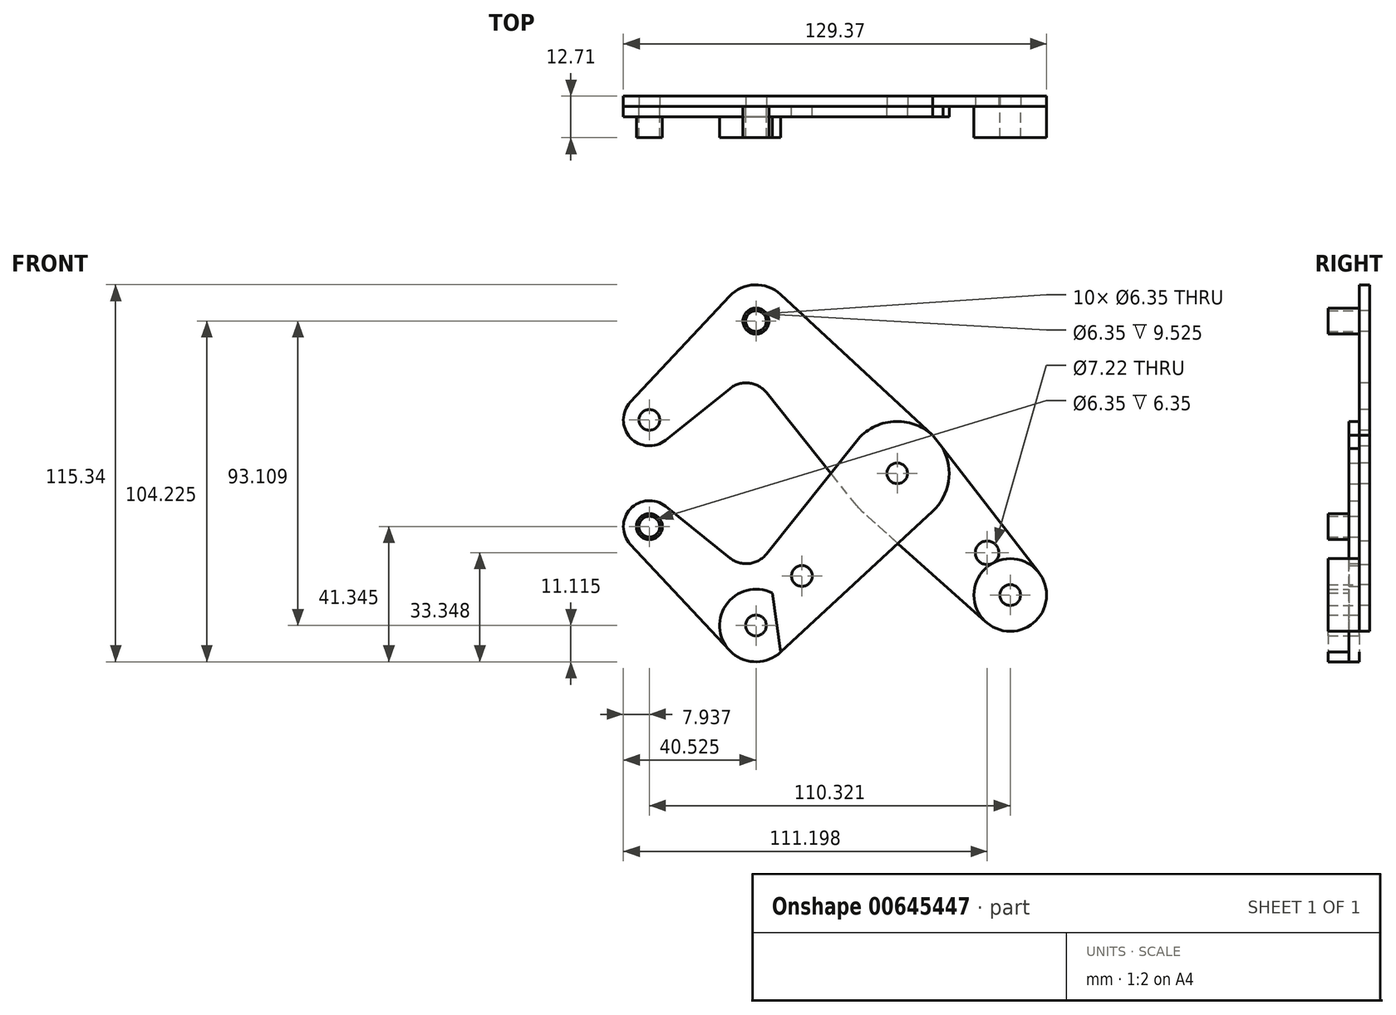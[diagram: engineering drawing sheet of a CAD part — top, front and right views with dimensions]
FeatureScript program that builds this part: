
annotation { "Feature Type Name" : "Feature", "Feature Type Description" : "" }
export const myFeature = defineFeature(function(context is Context, id is Id, definition is map)
    precondition{}
    {
        {
            var Q0;
            Q0=qCreatedBy(makeId("Front.planeOp"),FACE);
            var sketch = newSketch(context, id + "F0", { "sketchPlane" : qUnion([Q0])});
            skCircle(sketch, "E0", {"center": v(0, 0) * mm, "radius": 15.88 * mm});
            skLineSegment(sketch, "E1", {"start": v(0, 0) * mm, "end": v(-43.18, 46.55) * mm, "construction": true});
            skLineSegment(sketch, "E2", {"start": v(0, 0) * mm, "end": v(34.55, -37.24) * mm, "construction": true});
            skLineSegment(sketch, "E3", {"start": v(-43.18, 46.55) * mm, "end": v(-75.77, 16.33) * mm, "construction": true});
            skCircle(sketch, "E4", {"center": v(-43.18, 46.55) * mm, "radius": 11.11 * mm});
            skCircle(sketch, "E5", {"center": v(34.55, -37.24) * mm, "radius": 11.11 * mm});
            skCircle(sketch, "E6", {"center": v(34.55, -37.24) * mm, "radius": 3.18 * mm});
            skCircle(sketch, "E7", {"center": v(-75.77, 16.33) * mm, "radius": 7.94 * mm});
            skCircle(sketch, "E8", {"center": v(-43.18, 46.55) * mm, "radius": 3.18 * mm});
            skCircle(sketch, "E9", {"center": v(-75.77, 16.33) * mm, "radius": 3.18 * mm});
            skLineSegment(sketch, "E10", {"start": v(-81.57, 21.74) * mm, "end": v(-51.3, 54.14) * mm});
            skLineSegment(sketch, "E11", {"start": v(-35.63, 54.7) * mm, "end": v(10.8, 11.64) * mm});
            skLineSegment(sketch, "E12", {"start": v(10.8, 11.64) * mm, "end": v(43.34, -30.45) * mm});
            skLineSegment(sketch, "E13", {"start": v(0, 0) * mm, "end": v(-43.18, -46.55) * mm, "construction": true});
            skLineSegment(sketch, "E14", {"start": v(-43.18, -46.55) * mm, "end": v(-75.77, -16.33) * mm, "construction": true});
            skCircle(sketch, "E15", {"center": v(0, 0) * mm, "radius": 3.98 * mm});
            skCircle(sketch, "E16", {"center": v(0, 0) * mm, "radius": 3.18 * mm});
            skCircle(sketch, "E17", {"center": v(-43.18, -46.55) * mm, "radius": 11.11 * mm});
            skCircle(sketch, "E18", {"center": v(-43.18, -46.55) * mm, "radius": 3.18 * mm});
            skCircle(sketch, "E19", {"center": v(-75.77, -16.33) * mm, "radius": 7.94 * mm});
            skCircle(sketch, "E20", {"center": v(-75.77, -16.33) * mm, "radius": 3.18 * mm});
            skLineSegment(sketch, "E21", {"start": v(-70.8, 10.14) * mm, "end": v(-51.15, 25.91) * mm});
            skLineSegment(sketch, "E22", {"start": v(-12.42, -9.9) * mm, "end": v(-39.95, 24.67) * mm});
            skArc(sketch, "E23.filletArc", {"start": v(-39.95, 24.67) * mm, "mid": v(-45.3, 27.61) * mm, "end": v(-51.15, 25.91) * mm});
            skLineSegment(sketch, "E24", {"start": v(-12.42, 9.9) * mm, "end": v(-39.95, -24.67) * mm});
            skLineSegment(sketch, "E25", {"start": v(-70.8, -10.14) * mm, "end": v(-51.15, -25.91) * mm});
            skLineSegment(sketch, "E26", {"start": v(-81.57, -21.74) * mm, "end": v(-51.3, -54.14) * mm});
            skLineSegment(sketch, "E27", {"start": v(-35.63, -54.7) * mm, "end": v(10.8, -11.64) * mm});
            skArc(sketch, "E28.filletArc", {"start": v(-51.15, -25.91) * mm, "mid": v(-45.3, -27.61) * mm, "end": v(-39.95, -24.67) * mm});
            skLineSegment(sketch, "E29", {"start": v(27.15, -45.53) * mm, "end": v(-10.58, -11.84) * mm});
            skLineSegment(sketch, "E30", {"start": v(-75.77, 16.33) * mm, "end": v(-75.77, -16.33) * mm, "construction": true});
            skCircle(sketch, "E31", {"center": v(-29.14, -31.42) * mm, "radius": 3.18 * mm});
            skPoint(sketch, "E32", {"position": v(27.49, -24.32) * mm});
            skCircle(sketch, "E33", {"center": v(27.49, -24.32) * mm, "radius": 3.61 * mm});
            skLineSegment(sketch, "E34", {"start": v(27.49, -24.32) * mm, "end": v(24.84, -26.78) * mm, "construction": true});
            skSolve(sketch);
        }
        {
            var Q0;
            {var subQ0=sQuery(id+"F0.wireOp",EDGE,"E10");Q0=makeQuery(id+"F0.imprint","IMPRINT",FACE,{"disambiguationData":[TD([[makeQuery(id+"F0.imprint","IMPRINT",EDGE,{"derivedFrom":subQ0}),-1.0]])]});}
            var Q1;
            Q1=makeQuery(id+"F0.imprint","IMPRINT",FACE,{"disambiguationData":[TD([[makeQuery(id+"F0.imprint","IMPRINT",EDGE,{"derivedFrom":sQuery(id+"F0.wireOp",EDGE,"E9")}),-1.0]])]});
            var Q2;
            Q2=makeQuery(id+"F0.imprint","IMPRINT",FACE,{"disambiguationData":[TD([[makeQuery(id+"F0.imprint","IMPRINT",EDGE,{"derivedFrom":sQuery(id+"F0.wireOp",EDGE,"E8")}),-1.0]])]});
            var Q3;
            {var subQ5=sQuery(id+"F0.wireOp",EDGE,"E33");Q3=makeQuery(id+"F0.imprint","IMPRINT",FACE,{"disambiguationData":[TD([[makeQuery(id+"F0.imprint","IMPRINT",EDGE,{"derivedFrom":subQ5}),-1.0]])]});}
            var Q4;
            Q4=makeQuery(id+"F0.imprint","IMPRINT",FACE,{"disambiguationData":[TD([[makeQuery(id+"F0.imprint","IMPRINT",EDGE,{"derivedFrom":sQuery(id+"F0.wireOp",EDGE,"E15")}),-1.0]])]});
            var Q5;
            Q5=makeQuery(id+"F0.imprint","IMPRINT",FACE,{"disambiguationData":[TD([[makeQuery(id+"F0.imprint","IMPRINT",EDGE,{"derivedFrom":sQuery(id+"F0.wireOp",EDGE,"E6")}),-1.0]])]});
            var Q6;
            {var subQ0=sQuery(id+"F0.wireOp",EDGE,"E22");var subQ1=sQuery(id+"F0.wireOp",EDGE,"E0");var subQ2=makeQuery(id+"F0.imprint","INTERSECT",VERTEX,{"derivedFrom":[subQ1,subQ0]});Q6=makeQuery(id+"F0.imprint","IMPRINT",FACE,{"disambiguationData":[TD([[makeQuery(id+"F0.imprint","IMPRINT",EDGE,{"disambiguationData":[TD([[subQ2,1.0]])],"derivedFrom":subQ1}),-1.0]])]});}
            var Q7;
            {var subQ0=sQuery(id+"F0.wireOp",EDGE,"E27");var subQ1=sQuery(id+"F0.wireOp",EDGE,"E0");var subQ2=makeQuery(id+"F0.imprint","INTERSECT",VERTEX,{"derivedFrom":[subQ1,subQ0]});Q7=makeQuery(id+"F0.imprint","IMPRINT",FACE,{"disambiguationData":[TD([[makeQuery(id+"F0.imprint","IMPRINT",EDGE,{"disambiguationData":[TD([[subQ2,1.0]])],"derivedFrom":subQ1}),-1.0]])]});}
            var Q8;
            Q8=makeQuery(id+"F0.imprint","IMPRINT",FACE,{"disambiguationData":[TD([[makeQuery(id+"F0.imprint","IMPRINT",EDGE,{"derivedFrom":sQuery(id+"F0.wireOp",EDGE,"E15")}),1.0]])]});
            extrude(context, id + "F1", {"entities" : qUnion([Q0, Q1, Q2, Q3, Q4, Q5, Q6, Q7, Q8]), "oppositeDirection" : true, "depth" : 3.17 * mm, "offsetDistance" : 25.4 * mm});
        }
        {
            var Q0;
            {var subQ13=sQuery(id+"F0.wireOp",EDGE,"E25");Q0=makeQuery(id+"F0.imprint","IMPRINT",FACE,{"disambiguationData":[TD([[makeQuery(id+"F0.imprint","IMPRINT",EDGE,{"derivedFrom":subQ13}),-1.0]])]});}
            var Q1;
            Q1=makeQuery(id+"F0.imprint","IMPRINT",FACE,{"disambiguationData":[TD([[makeQuery(id+"F0.imprint","IMPRINT",EDGE,{"derivedFrom":sQuery(id+"F0.wireOp",EDGE,"E20")}),-1.0]])]});
            var Q2;
            Q2=makeQuery(id+"F0.imprint","IMPRINT",FACE,{"disambiguationData":[TD([[makeQuery(id+"F0.imprint","IMPRINT",EDGE,{"derivedFrom":sQuery(id+"F0.wireOp",EDGE,"E18")}),-1.0]])]});
            var Q3;
            {var subQ0=sQuery(id+"F0.wireOp",EDGE,"E22");var subQ1=sQuery(id+"F0.wireOp",EDGE,"E0");var subQ2=makeQuery(id+"F0.imprint","INTERSECT",VERTEX,{"derivedFrom":[subQ1,subQ0]});Q3=makeQuery(id+"F0.imprint","IMPRINT",FACE,{"disambiguationData":[TD([[makeQuery(id+"F0.imprint","IMPRINT",EDGE,{"disambiguationData":[TD([[subQ2,1.0]])],"derivedFrom":subQ1}),-1.0]])]});}
            var Q4;
            Q4=makeQuery(id+"F0.imprint","IMPRINT",FACE,{"disambiguationData":[TD([[makeQuery(id+"F0.imprint","IMPRINT",EDGE,{"derivedFrom":sQuery(id+"F0.wireOp",EDGE,"E15")}),-1.0]])]});
            var Q5;
            {var subQ0=sQuery(id+"F0.wireOp",EDGE,"E27");var subQ1=sQuery(id+"F0.wireOp",EDGE,"E0");var subQ2=makeQuery(id+"F0.imprint","INTERSECT",VERTEX,{"derivedFrom":[subQ1,subQ0]});Q5=makeQuery(id+"F0.imprint","IMPRINT",FACE,{"disambiguationData":[TD([[makeQuery(id+"F0.imprint","IMPRINT",EDGE,{"disambiguationData":[TD([[subQ2,1.0]])],"derivedFrom":subQ1}),-1.0]])]});}
            var Q6;
            Q6=makeQuery(id+"F0.imprint","IMPRINT",FACE,{"disambiguationData":[TD([[makeQuery(id+"F0.imprint","IMPRINT",EDGE,{"derivedFrom":sQuery(id+"F0.wireOp",EDGE,"E15")}),1.0]])]});
            extrude(context, id + "F2", {"entities" : qUnion([Q0, Q1, Q2, Q3, Q4, Q5, Q6]), "depth" : 3.17 * mm, "offsetDistance" : 25.4 * mm});
        }
        {
            var Q0;
            Q0=makeQuery(id+"F1.opExtrude","CAP_FACE",FACE,{"disambiguationData":[OSD([sQuery(id+"F0.wireOp",EDGE,"E0"),sQuery(id+"F0.wireOp",EDGE,"E4"),sQuery(id+"F0.wireOp",EDGE,"E5"),sQuery(id+"F0.wireOp",EDGE,"E6"),sQuery(id+"F0.wireOp",EDGE,"E7"),sQuery(id+"F0.wireOp",EDGE,"E8"),sQuery(id+"F0.wireOp",EDGE,"E9"),sQuery(id+"F0.wireOp",EDGE,"E10"),sQuery(id+"F0.wireOp",EDGE,"E11"),sQuery(id+"F0.wireOp",EDGE,"E12"),sQuery(id+"F0.wireOp",EDGE,"E16"),sQuery(id+"F0.wireOp",EDGE,"E21"),sQuery(id+"F0.wireOp",EDGE,"E22"),sQuery(id+"F0.wireOp",EDGE,"E23.filletArc"),sQuery(id+"F0.wireOp",EDGE,"E29"),sQuery(id+"F0.wireOp",EDGE,"E33")])],"isStart":true});
            var sketch = newSketch(context, id + "F3", { "sketchPlane" : qUnion([Q0])});
            skCircle(sketch, "E35", {"center": v(-43.18, 46.55) * mm, "radius": 3.98 * mm});
            skCircle(sketch, "E36", {"center": v(34.55, -37.24) * mm, "radius": 11.11 * mm});
            skCircle(sketch, "E37", {"center": v(0, 0) * mm, "radius": 3.98 * mm});
            skCircle(sketch, "E38.0", {"center": v(-43.18, 46.55) * mm, "radius": 3.18 * mm});
            skSolve(sketch);
        }
        {
            var Q0;
            Q0=makeQuery(id+"F2.opExtrude","CAP_FACE",FACE,{"disambiguationData":[OSD([sQuery(id+"F0.wireOp",EDGE,"E0"),sQuery(id+"F0.wireOp",EDGE,"E12"),sQuery(id+"F0.wireOp",EDGE,"E16"),sQuery(id+"F0.wireOp",EDGE,"E17"),sQuery(id+"F0.wireOp",EDGE,"E18"),sQuery(id+"F0.wireOp",EDGE,"E19"),sQuery(id+"F0.wireOp",EDGE,"E20"),sQuery(id+"F0.wireOp",EDGE,"E24"),sQuery(id+"F0.wireOp",EDGE,"E25"),sQuery(id+"F0.wireOp",EDGE,"E26"),sQuery(id+"F0.wireOp",EDGE,"E27"),sQuery(id+"F0.wireOp",EDGE,"E28.filletArc"),sQuery(id+"F0.wireOp",EDGE,"E31")])],"isStart":false});
            var sketch = newSketch(context, id + "F4", { "sketchPlane" : qUnion([Q0])});
            skCircle(sketch, "E39", {"center": v(-75.77, -16.33) * mm, "radius": 3.98 * mm});
            skCircle(sketch, "E40", {"center": v(-43.18, -46.55) * mm, "radius": 11.11 * mm});
            skPoint(sketch, "E41.0", {"position": v(34.55, -37.24) * mm});
            skLineSegment(sketch, "E42", {"start": v(-38.17, -36.64) * mm, "end": v(-35.63, -54.7) * mm});
            skLineSegment(sketch, "E43", {"start": v(-36.9, -45.67) * mm, "end": v(34.55, -37.24) * mm, "construction": true});
            skSolve(sketch);
        }
        {
            var Q0;
            Q0=qCreatedBy(makeId("Front.planeOp"),FACE);
            cPlane(context, id + "F5", {"entities" : qUnion([Q0]), "cplaneType" : CPlaneType.OFFSET, "offset" : 9.52 * mm, "width" : 152.4 * mm, "height" : 152.4 * mm});
        }
        {
            var Q0;
            {var subQ2=sQuery(id+"F4.wireOp",EDGE,"E42");Q0=makeQuery(id+"F4.imprint","IMPRINT",FACE,{"disambiguationData":[TD([[makeQuery(id+"F4.imprint","IMPRINT",EDGE,{"derivedFrom":subQ2}),-1.0]])]});}
            var Q1;
            Q1=makeQuery(id+"F0.imprint","IMPRINT",FACE,{"disambiguationData":[TD([[makeQuery(id+"F0.imprint","IMPRINT",EDGE,{"derivedFrom":sQuery(id+"F0.wireOp",EDGE,"E6")}),-1.0]])]});
            var Q2;
            Q2=makeQuery(id+"F4.imprint","IMPRINT",FACE,{"disambiguationData":[TD([[makeQuery(id+"F4.imprint","IMPRINT",EDGE,{"derivedFrom":sQuery(id+"F4.wireOp",EDGE,"E39")}),1.0]])]});
            var Q3;
            Q3=makeQuery(id+"F0.imprint","IMPRINT",FACE,{"disambiguationData":[TD([[makeQuery(id+"F0.imprint","IMPRINT",EDGE,{"derivedFrom":sQuery(id+"F0.wireOp",EDGE,"E8")}),1.0]])]});
            var Q4;
            Q4=makeQuery(id+"F3.imprint","IMPRINT",FACE,{"disambiguationData":[TD([[makeQuery(id+"F3.imprint","IMPRINT",EDGE,{"derivedFrom":sQuery(id+"F3.wireOp",EDGE,"E35")}),1.0]])]});
            var Q5;
            Q5=qCreatedBy(id+"F5.planeOp",FACE);
            extrude(context, id + "F6", {"entities" : qUnion([Q0, Q1, Q2, Q3, Q4]), "endBound" : BoundingType.UP_TO_SURFACE, "depth" : 25.4 * mm, "endBoundEntityFace" : qUnion([Q5]), "offsetDistance" : 25.4 * mm});
        }
    });
